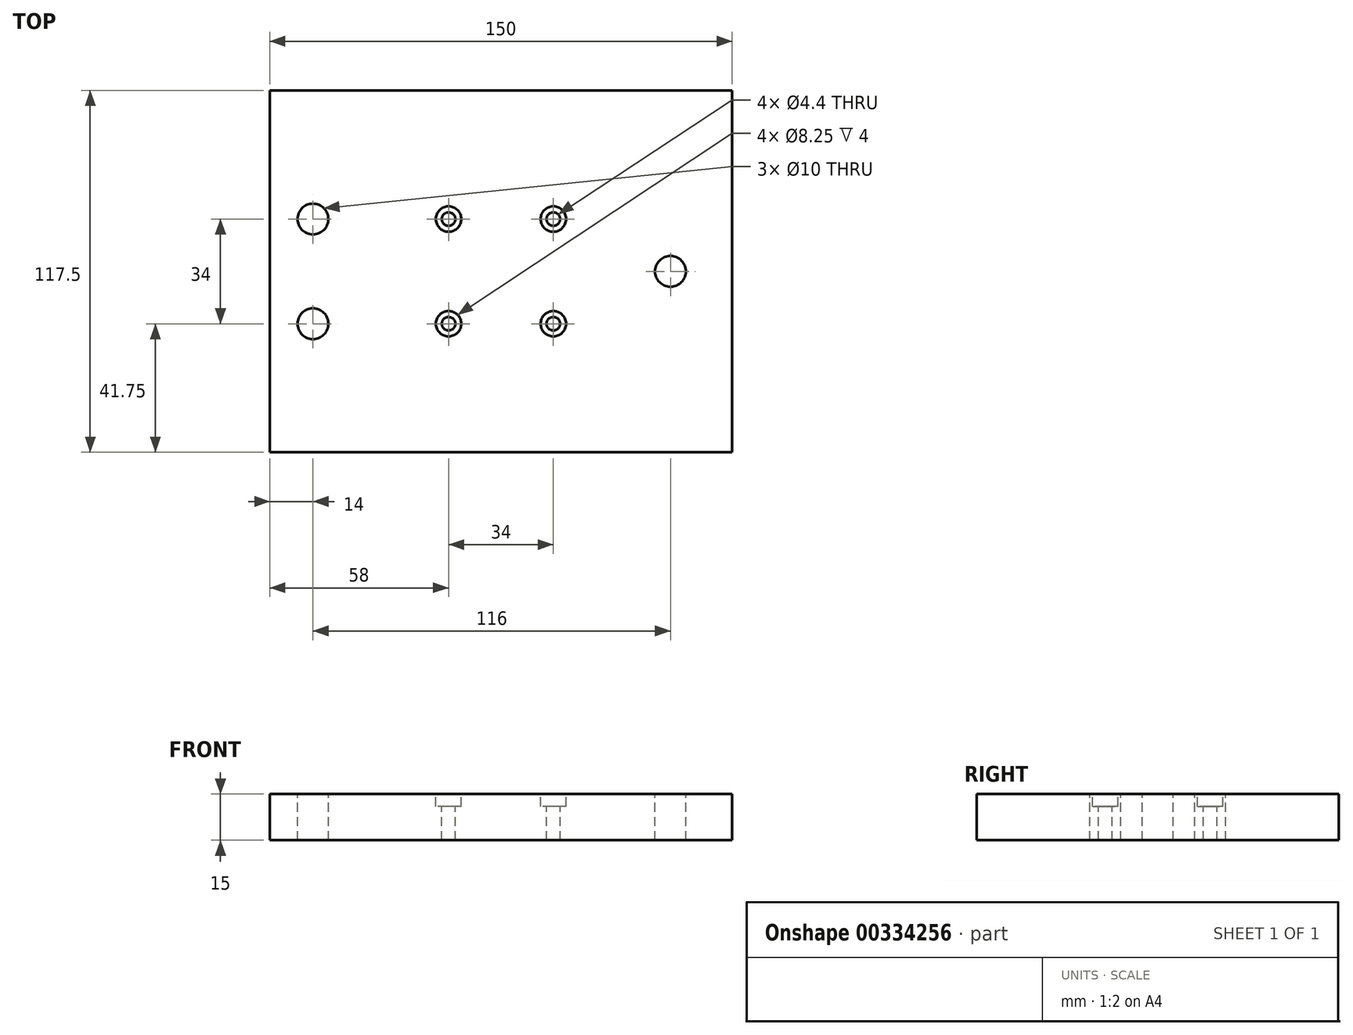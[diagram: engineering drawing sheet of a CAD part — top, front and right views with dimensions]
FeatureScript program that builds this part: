
annotation { "Feature Type Name" : "Feature", "Feature Type Description" : "" }
export const myFeature = defineFeature(function(context is Context, id is Id, definition is map)
    precondition{}
    {
        {
            var Q0;
            Q0=qCreatedBy(makeId("Top.planeOp"),FACE);
            var sketch = newSketch(context, id + "F0", { "sketchPlane" : qUnion([Q0])});
            skLineSegment(sketch, "E0.bottom", {"start": v(-75, 58.75) * mm, "end": v(75, 58.75) * mm});
            skLineSegment(sketch, "E0.top", {"start": v(-75, -58.75) * mm, "end": v(75, -58.75) * mm});
            skLineSegment(sketch, "E0.left", {"start": v(-75, 58.75) * mm, "end": v(-75, -58.75) * mm});
            skLineSegment(sketch, "E0.right", {"start": v(75, 58.75) * mm, "end": v(75, -58.75) * mm});
            skPoint(sketch, "E0.middle", {"position": v(0, 0) * mm});
            skSolve(sketch);
        }
        {
            var Q0;
            Q0 = qSketchRegion(id + "F0", true);
            extrude(context, id + "F1", {"entities" : qUnion([Q0]), "depth" : 15 * mm});
        }
        {
            var Q0;
            Q0=makeQuery(id+"F1.opExtrude","CAP_FACE",FACE,{"disambiguationData":[OSD([sQuery(id+"F0.wireOp",EDGE,"E0.bottom"),sQuery(id+"F0.wireOp",EDGE,"E0.top"),sQuery(id+"F0.wireOp",EDGE,"E0.left"),sQuery(id+"F0.wireOp",EDGE,"E0.right")])],"isStart":false});
            var sketch = newSketch(context, id + "F2", { "sketchPlane" : qUnion([Q0])});
            skPoint(sketch, "E1", {"position": v(55, 0) * mm});
            skPoint(sketch, "E2", {"position": v(-61, 17) * mm});
            skPoint(sketch, "E3", {"position": v(-61, -17) * mm});
            skLineSegment(sketch, "E4", {"start": v(-61, 17) * mm, "end": v(-61, -17) * mm, "construction": true});
            skPoint(sketch, "E5", {"position": v(-61, 0) * mm});
            skSolve(sketch);
        }
        {
            var Q0;
            Q0=sQuery(id+"F2.wireOp",VERTEX,"E2");
            var Q1;
            Q1=sQuery(id+"F2.wireOp",VERTEX,"E3");
            var Q2;
            Q2=sQuery(id+"F2.wireOp",VERTEX,"E1");
            var Q3;
            Q3=makeQuery(id+"F1.opExtrude","SWEPT_BODY",BODY,{"disambiguationData":[OSD([sQuery(id+"F0.wireOp",EDGE,"E0.bottom"),sQuery(id+"F0.wireOp",EDGE,"E0.top"),sQuery(id+"F0.wireOp",EDGE,"E0.left"),sQuery(id+"F0.wireOp",EDGE,"E0.right")])]});
            hole(context, id + "F3", {"style" : HoleStyle.SIMPLE, "endStyle" : HoleEndStyle.THROUGH, "standardTappedOrClearance" : lookupTablePath({ "standard" : "ISO", "size" : "10", "type" : "Drilled" }), "standardBlindInLast" : lookupTablePath({ "standard" : "ISO", "size" : "10", "type" : "Drilled" }), "holeDiameter" : 10 * mm, "tappedDepth" : 12 * mm, "tapClearance" : 3, "locations" : qUnion([Q0, Q1, Q2]), "scope" : qUnion([Q3])});
        }
        {
            var Q0;
            Q0=makeQuery(id+"F1.opExtrude","CAP_FACE",FACE,{"disambiguationData":[OSD([sQuery(id+"F0.wireOp",EDGE,"E0.bottom"),sQuery(id+"F0.wireOp",EDGE,"E0.top"),sQuery(id+"F0.wireOp",EDGE,"E0.left"),sQuery(id+"F0.wireOp",EDGE,"E0.right")])],"isStart":false});
            var sketch = newSketch(context, id + "F4", { "sketchPlane" : qUnion([Q0])});
            skLineSegment(sketch, "E6.bottom", {"start": v(-17, 17) * mm, "end": v(17, 17) * mm});
            skLineSegment(sketch, "E6.top", {"start": v(-17, -17) * mm, "end": v(17, -17) * mm});
            skLineSegment(sketch, "E6.left", {"start": v(-17, 17) * mm, "end": v(-17, -17) * mm});
            skLineSegment(sketch, "E6.right", {"start": v(17, 17) * mm, "end": v(17, -17) * mm});
            skPoint(sketch, "E6.middle", {"position": v(0, 0) * mm});
            skSolve(sketch);
        }
        {
            var Q0;
            Q0=sQuery(id+"F4.wireOp",VERTEX,"E6.bottom.start");
            var Q1;
            Q1=sQuery(id+"F4.wireOp",VERTEX,"E6.bottom.end");
            var Q2;
            Q2=sQuery(id+"F4.wireOp",VERTEX,"E6.top.end");
            var Q3;
            Q3=sQuery(id+"F4.wireOp",VERTEX,"E6.top.start");
            var Q4;
            Q4=makeQuery(id+"F1.opExtrude","SWEPT_BODY",BODY,{"disambiguationData":[OSD([sQuery(id+"F0.wireOp",EDGE,"E0.bottom"),sQuery(id+"F0.wireOp",EDGE,"E0.top"),sQuery(id+"F0.wireOp",EDGE,"E0.left"),sQuery(id+"F0.wireOp",EDGE,"E0.right")])]});
            hole(context, id + "F5", {"style" : HoleStyle.C_BORE, "endStyle" : HoleEndStyle.THROUGH, "standardTappedOrClearance" : lookupTablePath({ "standard" : "ISO", "fit" : "Normal", "size" : "M4", "type" : "Clearance" }), "standardBlindInLast" : lookupTablePath({ "fit" : "Standard", "standard" : "ISO", "size" : "M4", "type" : "Clearance" }), "holeDiameter" : 4.4 * mm, "cBoreDiameter" : 8.25 * mm, "cBoreDepth" : 4 * mm, "tappedDepth" : 12 * mm, "tapClearance" : 3, "locations" : qUnion([Q0, Q1, Q2, Q3]), "scope" : qUnion([Q4])});
        }
    });
